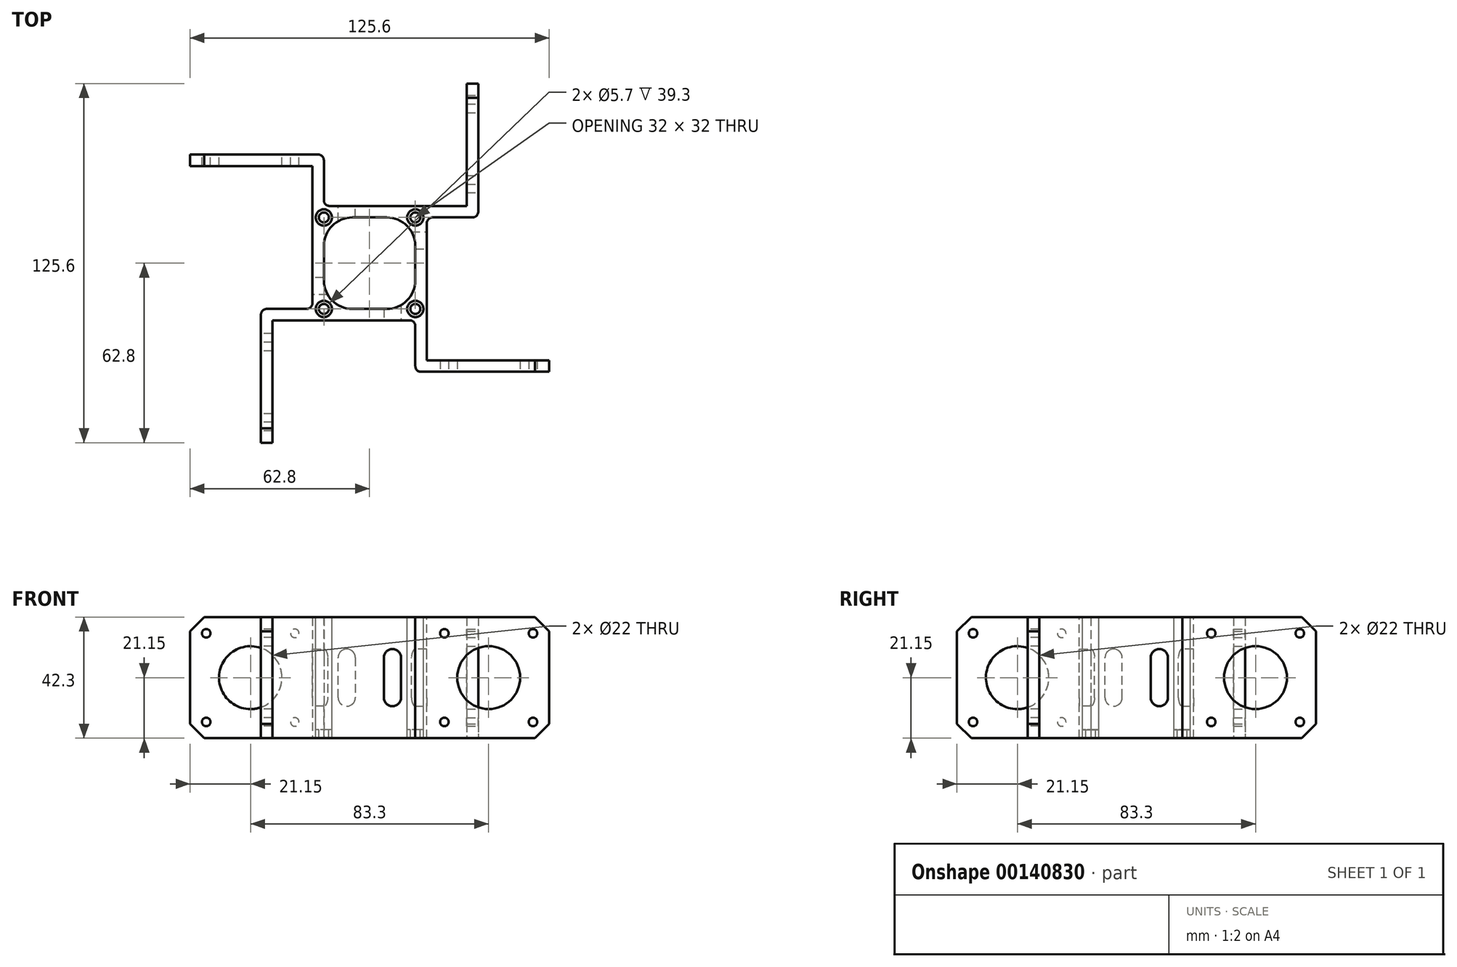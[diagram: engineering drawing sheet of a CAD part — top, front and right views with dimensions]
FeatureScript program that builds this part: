
annotation { "Feature Type Name" : "Feature", "Feature Type Description" : "" }
export const myFeature = defineFeature(function(context is Context, id is Id, definition is map)
    precondition{}
    {
        {
            var Q0;
            Q0=qCreatedBy(makeId("Top.planeOp"),FACE);
            var sketch = newSketch(context, id + "F0", { "sketchPlane" : qUnion([Q0])});
            skLineSegment(sketch, "E0", {"start": v(-20, -4) * mm, "end": v(-20, -56) * mm});
            skLineSegment(sketch, "E1", {"start": v(-20, -56) * mm, "end": v(-16, -56) * mm});
            skLineSegment(sketch, "E2", {"start": v(-16, -56) * mm, "end": v(-16, 0) * mm});
            skLineSegment(sketch, "E3", {"start": v(-20, -4) * mm, "end": v(-20.5, -4) * mm});
            skLineSegment(sketch, "E4", {"start": v(-20.5, -4) * mm, "end": v(-20.5, 0) * mm});
            skLineSegment(sketch, "E5", {"start": v(-20.5, 0) * mm, "end": v(-16, 0) * mm});
            skSolve(sketch);
        }
        {
            var Q0;
            Q0=qCreatedBy(makeId("Front.planeOp"),FACE);
            var sketch = newSketch(context, id + "F1", { "sketchPlane" : qUnion([Q0])});
            skLineSegment(sketch, "E6.0", {"start": v(-25.5, 21.15) * mm, "end": v(-57.8, 21.15) * mm});
            skLineSegment(sketch, "E6.1", {"start": v(-57.8, 21.15) * mm, "end": v(-62.8, 16.15) * mm});
            skLineSegment(sketch, "E6.2", {"start": v(-62.8, 16.15) * mm, "end": v(-62.8, -16.15) * mm});
            skLineSegment(sketch, "E6.3", {"start": v(-62.8, -16.15) * mm, "end": v(-57.8, -21.15) * mm});
            skLineSegment(sketch, "E6.4", {"start": v(-57.8, -21.15) * mm, "end": v(-25.5, -21.15) * mm});
            skLineSegment(sketch, "E6.6", {"start": v(-20.5, -16.15) * mm, "end": v(-20.5, 16.15) * mm});
            skCircle(sketch, "E6.8", {"center": v(-26.15, 15.5) * mm, "radius": 1.5 * mm});
            skCircle(sketch, "E6.9", {"center": v(-26.15, -15.5) * mm, "radius": 1.5 * mm});
            skCircle(sketch, "E6.10", {"center": v(-41.65, 0) * mm, "radius": 11 * mm});
            skCircle(sketch, "E6.11", {"center": v(-57.15, 15.5) * mm, "radius": 1.5 * mm});
            skCircle(sketch, "E6.12", {"center": v(-57.15, -15.5) * mm, "radius": 1.5 * mm});
            skLineSegment(sketch, "E7", {"start": v(-25.5, 21.15) * mm, "end": v(-20.5, 21.15) * mm});
            skLineSegment(sketch, "E8", {"start": v(-20.5, 21.15) * mm, "end": v(-20.5, 16.15) * mm});
            skLineSegment(sketch, "E9", {"start": v(-20.5, -16.15) * mm, "end": v(-20.5, -21.15) * mm});
            skLineSegment(sketch, "E10", {"start": v(-20.5, -21.15) * mm, "end": v(-25.5, -21.15) * mm});
            skSolve(sketch);
        }
        {
            var Q0;
            Q0=makeQuery(id+"F0.imprint","IMPRINT",FACE,{"disambiguationData":[TD([[makeQuery(id+"F0.imprint","IMPRINT",EDGE,{"derivedFrom":sQuery(id+"F0.wireOp",EDGE,"E0")}),1.0]])]});
            extrude(context, id + "F2", {"entities" : qUnion([Q0]), "endBound" : BoundingType.SYMMETRIC, "depth" : 42.3 * mm});
        }
        {
            var Q0;
            Q0=makeQuery(id+"F1.imprint","IMPRINT",FACE,{"disambiguationData":[TD([[makeQuery(id+"F1.imprint","IMPRINT",EDGE,{"derivedFrom":sQuery(id+"F1.wireOp",EDGE,"E6.0")}),1.0]])]});
            extrude(context, id + "F3", {"entities" : qUnion([Q0]), "operationType" : NewBodyOperationType.ADD, "depth" : 4 * mm});
        }
        {
            var Q0;
            Q0=makeQuery(id+"F2.opExtrude","SWEPT_EDGE",EDGE,{"disambiguationData":[OSD([sQuery(id+"F0.wireOp",EDGE,"E2"),sQuery(id+"F0.wireOp",EDGE,"E5")])]});
            fillet(context, id + "F4", {"entities" : qUnion([Q0]), "radius" : 2 * mm, "tangentPropagation" : true, "allowEdgeOverflow" : false});
        }
        {
            var Q0;
            Q0=makeQuery(id+"F2.opExtrude","SWEPT_FACE",FACE,{"disambiguationData":[OSD([sQuery(id+"F0.wireOp",EDGE,"E0")])]});
            var sketch = newSketch(context, id + "F5", { "sketchPlane" : qUnion([Q0])});
            skLineSegment(sketch, "E11.bottom", {"start": v(49, -10) * mm, "end": v(43, -10) * mm});
            skLineSegment(sketch, "E11.top", {"start": v(49, 10) * mm, "end": v(43, 10) * mm});
            skLineSegment(sketch, "E11.left", {"start": v(49, -10) * mm, "end": v(49, 10) * mm});
            skLineSegment(sketch, "E11.right", {"start": v(43, -10) * mm, "end": v(43, 10) * mm});
            skPoint(sketch, "E11.middle", {"position": v(46, 0) * mm});
            skSolve(sketch);
        }
        {
            var Q0;
            Q0=makeQuery(id+"F5.imprint","IMPRINT",FACE,{"disambiguationData":[TD([[makeQuery(id+"F5.imprint","IMPRINT",EDGE,{"derivedFrom":sQuery(id+"F5.wireOp",EDGE,"E11.bottom")}),-1.0]])]});
            var Q1;
            Q1=makeQuery(id+"F2.opExtrude","SWEPT_FACE",FACE,{"disambiguationData":[OSD([sQuery(id+"F0.wireOp",EDGE,"E2")])]});
            extrude(context, id + "F6", {"entities" : qUnion([Q0]), "operationType" : NewBodyOperationType.REMOVE, "endBound" : BoundingType.UP_TO_SURFACE, "oppositeDirection" : true, "endBoundEntityFace" : qUnion([Q1]), "depth" : 25 * mm});
        }
        {
            var Q0;
            Q0=makeQuery(id+"F6.boolean.opBoolean","COPY",EDGE,{"derivedFrom":makeQuery(id+"F6.opExtrude","SWEPT_EDGE",EDGE,{"disambiguationData":[OSD([sQuery(id+"F5.wireOp",EDGE,"E11.bottom"),sQuery(id+"F5.wireOp",EDGE,"E11.left")])]})});
            var Q1;
            Q1=makeQuery(id+"F6.boolean.opBoolean","COPY",EDGE,{"derivedFrom":makeQuery(id+"F6.opExtrude","SWEPT_EDGE",EDGE,{"disambiguationData":[OSD([sQuery(id+"F5.wireOp",EDGE,"E11.bottom"),sQuery(id+"F5.wireOp",EDGE,"E11.right")])]})});
            var Q2;
            Q2=makeQuery(id+"F6.boolean.opBoolean","COPY",EDGE,{"derivedFrom":makeQuery(id+"F6.opExtrude","SWEPT_EDGE",EDGE,{"disambiguationData":[OSD([sQuery(id+"F5.wireOp",EDGE,"E11.top"),sQuery(id+"F5.wireOp",EDGE,"E11.left")])]})});
            var Q3;
            Q3=makeQuery(id+"F6.boolean.opBoolean","COPY",EDGE,{"derivedFrom":makeQuery(id+"F6.opExtrude","SWEPT_EDGE",EDGE,{"disambiguationData":[OSD([sQuery(id+"F5.wireOp",EDGE,"E11.top"),sQuery(id+"F5.wireOp",EDGE,"E11.right")])]})});
            fillet(context, id + "F7", {"entities" : qUnion([Q0, Q1, Q2, Q3]), "radius" : 3 * mm, "tangentPropagation" : true, "allowEdgeOverflow" : false});
        }
        {
            var Q0;
            Q0=qCreatedBy(makeId("Right.planeOp"),FACE);
            var sketch = newSketch(context, id + "F8", { "sketchPlane" : qUnion([Q0])});
            skLineSegment(sketch, "E12", {"start": v(-38, 30.37) * mm, "end": v(-38, -31.22) * mm, "construction": true});
            skSolve(sketch);
        }
        {
            var Q0;
            Q0=makeQuery(id+"F2.opExtrude","SWEPT_BODY",BODY,{"disambiguationData":[OSD([sQuery(id+"F0.wireOp",EDGE,"E0"),sQuery(id+"F0.wireOp",EDGE,"E1"),sQuery(id+"F0.wireOp",EDGE,"E2"),sQuery(id+"F0.wireOp",EDGE,"E3"),sQuery(id+"F0.wireOp",EDGE,"E4"),sQuery(id+"F0.wireOp",EDGE,"E5")])]});
            var Q1;
            Q1=sQuery(id+"F8.wireOp",EDGE,"E12");
            circularPattern(context, id + "F9", {"operationType" : NewBodyOperationType.ADD, "entities" : qUnion([Q0]), "axis" : qUnion([Q1]), "angle" : 360 * degree, "instanceCount" : 4, "equalSpace" : true});
        }
        {
            var Q0;
            {var subQ0=makeQuery(id+"F2.opExtrude","SWEPT_FACE",FACE,{"disambiguationData":[OSD([sQuery(id+"F0.wireOp",EDGE,"E2")])]});Q0=makeQuery(id+"F9.boolean.opBoolean","INTERSECT",EDGE,{"derivedFrom":[subQ0,makeQuery(id+"F9.opPattern","COPY",FACE,{"derivedFrom":subQ0,"instanceName":"1"})]});}
            var Q1;
            {var subQ0=makeQuery(id+"F2.opExtrude","SWEPT_FACE",FACE,{"disambiguationData":[OSD([sQuery(id+"F0.wireOp",EDGE,"E2")])]});Q1=makeQuery(id+"F9.boolean.opBoolean","INTERSECT",EDGE,{"derivedFrom":[subQ0,makeQuery(id+"F9.opPattern","COPY",FACE,{"derivedFrom":subQ0,"instanceName":"3"})]});}
            var Q2;
            {var subQ0=makeQuery(id+"F2.opExtrude","SWEPT_FACE",FACE,{"disambiguationData":[OSD([sQuery(id+"F0.wireOp",EDGE,"E2")])]});Q2=makeQuery(id+"F9.boolean.opBoolean","INTERSECT",EDGE,{"derivedFrom":[makeQuery(id+"F9.opPattern","COPY",FACE,{"derivedFrom":subQ0,"instanceName":"2"}),makeQuery(id+"F9.opPattern","COPY",FACE,{"derivedFrom":subQ0,"instanceName":"3"})]});}
            var Q3;
            {var subQ0=makeQuery(id+"F2.opExtrude","SWEPT_FACE",FACE,{"disambiguationData":[OSD([sQuery(id+"F0.wireOp",EDGE,"E2")])]});Q3=makeQuery(id+"F9.boolean.opBoolean","INTERSECT",EDGE,{"derivedFrom":[makeQuery(id+"F9.opPattern","COPY",FACE,{"derivedFrom":subQ0,"instanceName":"1"}),makeQuery(id+"F9.opPattern","COPY",FACE,{"derivedFrom":subQ0,"instanceName":"2"})]});}
            fillet(context, id + "F10", {"entities" : qUnion([Q0, Q1, Q2, Q3]), "radius" : 10 * mm, "tangentPropagation" : true, "allowEdgeOverflow" : false});
        }
        {
            var Q0;
            Q0=makeQuery(id+"F9.boolean.opBoolean","INTERSECT",EDGE,{"derivedFrom":[makeQuery(id+"F2.opExtrude","SWEPT_FACE",FACE,{"disambiguationData":[OSD([sQuery(id+"F0.wireOp",EDGE,"E2")])]}),makeQuery(id+"F9.opPattern","COPY",FACE,{"derivedFrom":makeQuery(id+"F2.opExtrude","SWEPT_FACE",FACE,{"disambiguationData":[OSD([sQuery(id+"F0.wireOp",EDGE,"E0")])]}),"instanceName":"1"})]});
            var Q1;
            Q1=makeQuery(id+"F9.boolean.opBoolean","INTERSECT",EDGE,{"derivedFrom":[makeQuery(id+"F9.opPattern","COPY",FACE,{"derivedFrom":makeQuery(id+"F2.opExtrude","SWEPT_FACE",FACE,{"disambiguationData":[OSD([sQuery(id+"F0.wireOp",EDGE,"E2")])]}),"instanceName":"1"}),makeQuery(id+"F9.opPattern","COPY",FACE,{"derivedFrom":makeQuery(id+"F2.opExtrude","SWEPT_FACE",FACE,{"disambiguationData":[OSD([sQuery(id+"F0.wireOp",EDGE,"E0")])]}),"instanceName":"2"})]});
            var Q2;
            Q2=makeQuery(id+"F9.boolean.opBoolean","INTERSECT",EDGE,{"derivedFrom":[makeQuery(id+"F9.opPattern","COPY",FACE,{"derivedFrom":makeQuery(id+"F2.opExtrude","SWEPT_FACE",FACE,{"disambiguationData":[OSD([sQuery(id+"F0.wireOp",EDGE,"E2")])]}),"instanceName":"2"}),makeQuery(id+"F9.opPattern","COPY",FACE,{"derivedFrom":makeQuery(id+"F2.opExtrude","SWEPT_FACE",FACE,{"disambiguationData":[OSD([sQuery(id+"F0.wireOp",EDGE,"E0")])]}),"instanceName":"3"})]});
            var Q3;
            Q3=makeQuery(id+"F9.boolean.opBoolean","INTERSECT",EDGE,{"derivedFrom":[makeQuery(id+"F2.opExtrude","SWEPT_FACE",FACE,{"disambiguationData":[OSD([sQuery(id+"F0.wireOp",EDGE,"E0")])]}),makeQuery(id+"F9.opPattern","COPY",FACE,{"derivedFrom":makeQuery(id+"F2.opExtrude","SWEPT_FACE",FACE,{"disambiguationData":[OSD([sQuery(id+"F0.wireOp",EDGE,"E2")])]}),"instanceName":"3"})]});
            fillet(context, id + "F11", {"entities" : qUnion([Q0, Q1, Q2, Q3]), "radius" : 2 * mm, "tangentPropagation" : true, "allowEdgeOverflow" : false});
        }
        {
            var Q0;
            {var subQ0=makeQuery(id+"F3.boolean.opBoolean","MERGE",FACE,{"derivedFrom":[makeQuery(id+"F2.opExtrude","CAP_FACE",FACE,{"disambiguationData":[OSD([sQuery(id+"F0.wireOp",EDGE,"E0"),sQuery(id+"F0.wireOp",EDGE,"E1"),sQuery(id+"F0.wireOp",EDGE,"E2"),sQuery(id+"F0.wireOp",EDGE,"E3"),sQuery(id+"F0.wireOp",EDGE,"E4"),sQuery(id+"F0.wireOp",EDGE,"E5")])],"isStart":false}),makeQuery(id+"F3.opExtrude","SWEPT_FACE",FACE,{"disambiguationData":[OSD([sQuery(id+"F1.wireOp",EDGE,"E6.0"),sQuery(id+"F1.wireOp",EDGE,"E7")])]})]});Q0=makeQuery(id+"F9.boolean.opBoolean","MERGE",FACE,{"derivedFrom":[subQ0,makeQuery(id+"F9.opPattern","COPY",FACE,{"derivedFrom":subQ0,"instanceName":"1"}),makeQuery(id+"F9.opPattern","COPY",FACE,{"derivedFrom":subQ0,"instanceName":"2"}),makeQuery(id+"F9.opPattern","COPY",FACE,{"derivedFrom":subQ0,"instanceName":"3"})]});}
            var sketch = newSketch(context, id + "F12", { "sketchPlane" : qUnion([Q0])});
            skCircle(sketch, "E13", {"center": v(16, -22) * mm, "radius": 1.75 * mm});
            skLineSegment(sketch, "E14", {"start": v(0, -22) * mm, "end": v(0, -54) * mm, "construction": true});
            skLineSegment(sketch, "E15", {"start": v(-16, -38) * mm, "end": v(16, -38) * mm, "construction": true});
            skCircle(sketch, "E16.MirrorC", {"center": v(-16, -22) * mm, "radius": 1.75 * mm});
            skCircle(sketch, "E17.MirrorC", {"center": v(16, -54) * mm, "radius": 1.75 * mm});
            skCircle(sketch, "E18.MirrorC", {"center": v(-16, -54) * mm, "radius": 1.75 * mm});
            skCircle(sketch, "E19", {"center": v(-16, -22) * mm, "radius": 2.85 * mm});
            skCircle(sketch, "E20.MirrorC", {"center": v(16, -22) * mm, "radius": 2.85 * mm});
            skCircle(sketch, "E21.MirrorC", {"center": v(16, -54) * mm, "radius": 2.85 * mm});
            skCircle(sketch, "E22.MirrorC", {"center": v(-16, -54) * mm, "radius": 2.85 * mm});
            skSolve(sketch);
        }
        {
            var Q0;
            Q0=makeQuery(id+"F12.imprint","IMPRINT",FACE,{"disambiguationData":[TD([[makeQuery(id+"F12.imprint","IMPRINT",EDGE,{"derivedFrom":sQuery(id+"F12.wireOp",EDGE,"E13")}),1.0]])]});
            var Q1;
            Q1=makeQuery(id+"F12.imprint","IMPRINT",FACE,{"disambiguationData":[TD([[makeQuery(id+"F12.imprint","IMPRINT",EDGE,{"derivedFrom":sQuery(id+"F12.wireOp",EDGE,"E16.MirrorC")}),-1.0]])]});
            var Q2;
            Q2=makeQuery(id+"F12.imprint","IMPRINT",FACE,{"disambiguationData":[TD([[makeQuery(id+"F12.imprint","IMPRINT",EDGE,{"derivedFrom":sQuery(id+"F12.wireOp",EDGE,"E18.MirrorC")}),1.0]])]});
            var Q3;
            Q3=makeQuery(id+"F12.imprint","IMPRINT",FACE,{"disambiguationData":[TD([[makeQuery(id+"F12.imprint","IMPRINT",EDGE,{"derivedFrom":sQuery(id+"F12.wireOp",EDGE,"E17.MirrorC")}),-1.0]])]});
            var Q4;
            Q4=sQuery(id+"F12.wireOp",EDGE,"E16.MirrorC");
            var Q5;
            Q5=sQuery(id+"F12.wireOp",EDGE,"E13");
            var Q6;
            Q6=sQuery(id+"F12.wireOp",EDGE,"E17.MirrorC");
            var Q7;
            Q7=sQuery(id+"F12.wireOp",EDGE,"E18.MirrorC");
            var Q8;
            {var subQ0=makeQuery(id+"F3.boolean.opBoolean","MERGE",FACE,{"derivedFrom":[makeQuery(id+"F2.opExtrude","CAP_FACE",FACE,{"disambiguationData":[OSD([sQuery(id+"F0.wireOp",EDGE,"E0"),sQuery(id+"F0.wireOp",EDGE,"E1"),sQuery(id+"F0.wireOp",EDGE,"E2"),sQuery(id+"F0.wireOp",EDGE,"E3"),sQuery(id+"F0.wireOp",EDGE,"E4"),sQuery(id+"F0.wireOp",EDGE,"E5")])],"isStart":true}),makeQuery(id+"F3.opExtrude","SWEPT_FACE",FACE,{"disambiguationData":[OSD([sQuery(id+"F1.wireOp",EDGE,"E6.4"),sQuery(id+"F1.wireOp",EDGE,"E10")])]})]});Q8=makeQuery(id+"F9.boolean.opBoolean","MERGE",FACE,{"derivedFrom":[subQ0,makeQuery(id+"F9.opPattern","COPY",FACE,{"derivedFrom":subQ0,"instanceName":"1"}),makeQuery(id+"F9.opPattern","COPY",FACE,{"derivedFrom":subQ0,"instanceName":"2"}),makeQuery(id+"F9.opPattern","COPY",FACE,{"derivedFrom":subQ0,"instanceName":"3"})]});}
            extrude(context, id + "F13", {"entities" : qUnion([Q0, Q1, Q2, Q3]), "operationType" : NewBodyOperationType.REMOVE, "surfaceEntities" : qUnion([Q4, Q5, Q6, Q7]), "endBound" : BoundingType.UP_TO_SURFACE, "oppositeDirection" : true, "endBoundEntityFace" : qUnion([Q8]), "depth" : 39.3 * mm});
        }
        {
            var Q0;
            Q0=makeQuery(id+"F12.imprint","IMPRINT",FACE,{"disambiguationData":[TD([[makeQuery(id+"F12.imprint","IMPRINT",EDGE,{"derivedFrom":sQuery(id+"F12.wireOp",EDGE,"E16.MirrorC")}),1.0]])]});
            var Q1;
            Q1=makeQuery(id+"F12.imprint","IMPRINT",FACE,{"disambiguationData":[TD([[makeQuery(id+"F12.imprint","IMPRINT",EDGE,{"derivedFrom":sQuery(id+"F12.wireOp",EDGE,"E13")}),-1.0]])]});
            var Q2;
            Q2=makeQuery(id+"F12.imprint","IMPRINT",FACE,{"disambiguationData":[TD([[makeQuery(id+"F12.imprint","IMPRINT",EDGE,{"derivedFrom":sQuery(id+"F12.wireOp",EDGE,"E17.MirrorC")}),1.0]])]});
            var Q3;
            Q3=makeQuery(id+"F12.imprint","IMPRINT",FACE,{"disambiguationData":[TD([[makeQuery(id+"F12.imprint","IMPRINT",EDGE,{"derivedFrom":sQuery(id+"F12.wireOp",EDGE,"E18.MirrorC")}),-1.0]])]});
            extrude(context, id + "F14", {"entities" : qUnion([Q0, Q1, Q2, Q3]), "operationType" : NewBodyOperationType.REMOVE, "oppositeDirection" : true, "depth" : 39.3 * mm});
        }
    });
